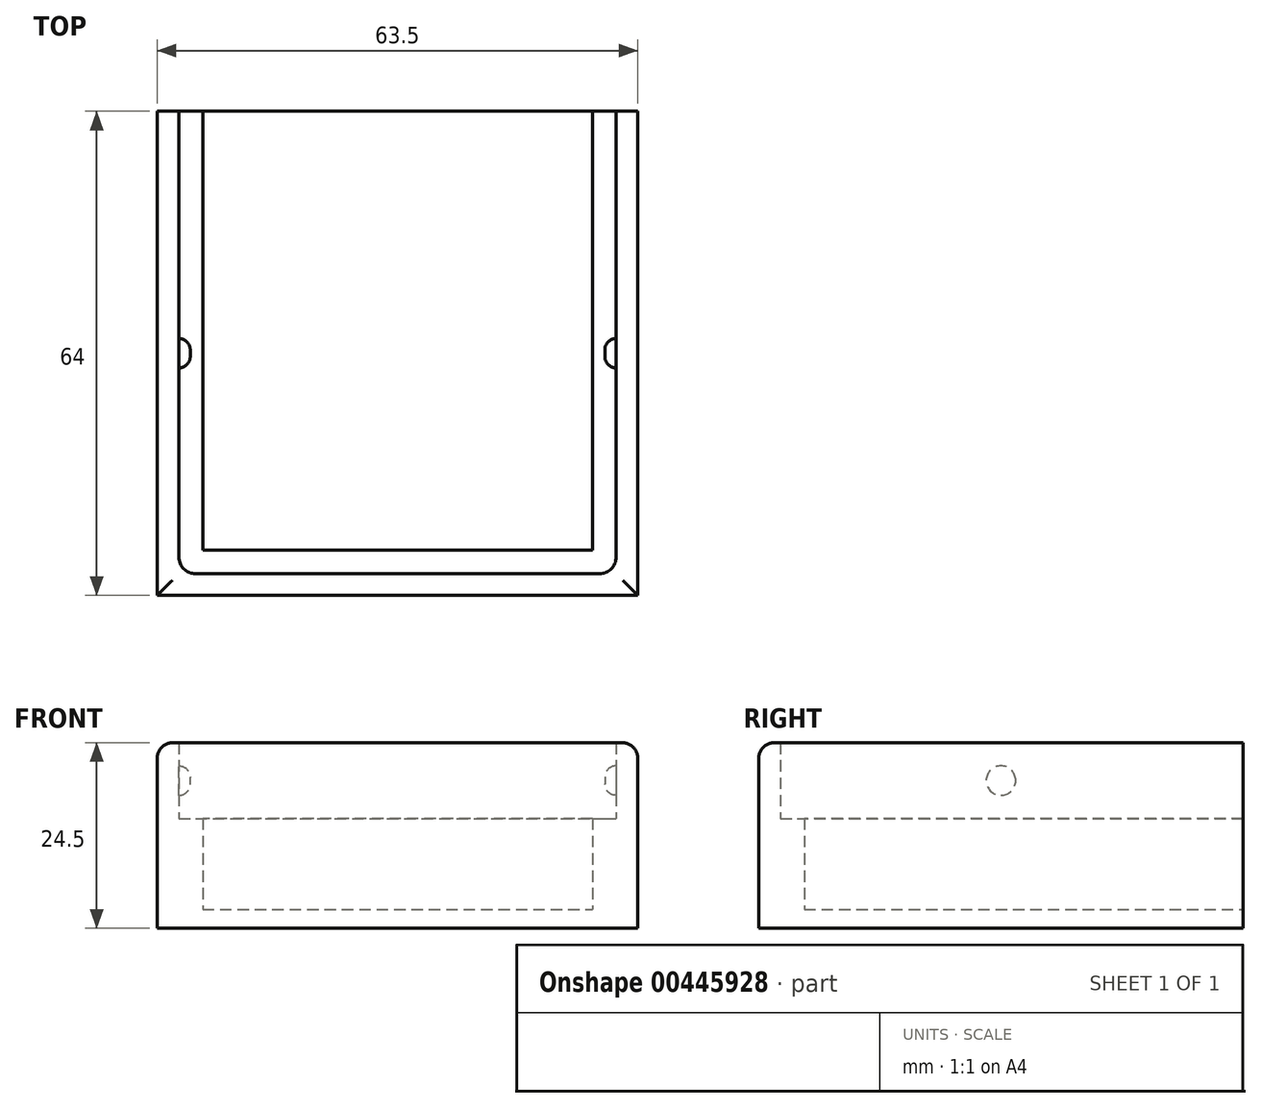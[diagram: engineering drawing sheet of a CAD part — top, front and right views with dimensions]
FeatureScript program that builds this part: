
annotation { "Feature Type Name" : "Feature", "Feature Type Description" : "" }
export const myFeature = defineFeature(function(context is Context, id is Id, definition is map)
    precondition{}
    {
        {
            var Q0;
            Q0=qCreatedBy(makeId("Top.planeOp"),FACE);
            var sketch = newSketch(context, id + "F0", { "sketchPlane" : qUnion([Q0])});
            skLineSegment(sketch, "E0.bottom", {"start": v(-31.75, 32) * mm, "end": v(31.75, 32) * mm});
            skLineSegment(sketch, "E0.top", {"start": v(-31.75, -32) * mm, "end": v(31.75, -32) * mm});
            skLineSegment(sketch, "E0.left", {"start": v(-31.75, 32) * mm, "end": v(-31.75, -32) * mm});
            skLineSegment(sketch, "E0.right", {"start": v(31.75, 32) * mm, "end": v(31.75, -32) * mm});
            skSolve(sketch);
        }
        {
            var Q0;
            Q0=makeQuery(id+"F0.imprint","IMPRINT",FACE,{"disambiguationData":[TD([[makeQuery(id+"F0.imprint","IMPRINT",EDGE,{"derivedFrom":sQuery(id+"F0.wireOp",EDGE,"E0.bottom")}),-1.0]])]});
            extrude(context, id + "F1", {"entities" : qUnion([Q0]), "depth" : 2.5 * mm});
        }
        {
            var Q0;
            Q0=makeQuery(id+"F1.opExtrude","CAP_FACE",FACE,{"disambiguationData":[OSD([sQuery(id+"F0.wireOp",EDGE,"E0.bottom"),sQuery(id+"F0.wireOp",EDGE,"E0.top"),sQuery(id+"F0.wireOp",EDGE,"E0.left"),sQuery(id+"F0.wireOp",EDGE,"E0.right")])],"isStart":false});
            var sketch = newSketch(context, id + "F2", { "sketchPlane" : qUnion([Q0])});
            skLineSegment(sketch, "E1", {"start": v(-31.75, 32) * mm, "end": v(-31.75, -32) * mm});
            skLineSegment(sketch, "E2", {"start": v(-31.75, -32) * mm, "end": v(31.75, -32) * mm});
            skLineSegment(sketch, "E3", {"start": v(31.75, -32) * mm, "end": v(31.75, 32) * mm});
            skLineSegment(sketch, "E4", {"start": v(31.75, 32) * mm, "end": v(25.75, 32) * mm});
            skLineSegment(sketch, "E5", {"start": v(25.75, 32) * mm, "end": v(25.75, -26) * mm});
            skLineSegment(sketch, "E6", {"start": v(25.75, -26) * mm, "end": v(-25.75, -26) * mm});
            skLineSegment(sketch, "E7", {"start": v(-25.75, -26) * mm, "end": v(-25.75, 32) * mm});
            skLineSegment(sketch, "E8", {"start": v(-25.75, 32) * mm, "end": v(-31.75, 32) * mm});
            skSolve(sketch);
        }
        {
            var Q0;
            Q0 = qSketchRegion(id + "F2", true);
            extrude(context, id + "F3", {"entities" : qUnion([Q0]), "operationType" : NewBodyOperationType.ADD, "depth" : 12 * mm});
        }
        {
            var Q0;
            Q0=makeQuery(id+"F3.opExtrude","CAP_FACE",FACE,{"disambiguationData":[OSD([sQuery(id+"F2.wireOp",EDGE,"E1"),sQuery(id+"F2.wireOp",EDGE,"E2"),sQuery(id+"F2.wireOp",EDGE,"E3"),sQuery(id+"F2.wireOp",EDGE,"E4"),sQuery(id+"F2.wireOp",EDGE,"E5"),sQuery(id+"F2.wireOp",EDGE,"E6"),sQuery(id+"F2.wireOp",EDGE,"E7"),sQuery(id+"F2.wireOp",EDGE,"E8")])],"isStart":false});
            var sketch = newSketch(context, id + "F4", { "sketchPlane" : qUnion([Q0])});
            skLineSegment(sketch, "E9", {"start": v(-31.75, 32) * mm, "end": v(-31.75, -32) * mm});
            skLineSegment(sketch, "E10", {"start": v(-31.75, -32) * mm, "end": v(31.75, -32) * mm});
            skLineSegment(sketch, "E11", {"start": v(31.75, -32) * mm, "end": v(31.75, 32) * mm});
            skLineSegment(sketch, "E12", {"start": v(-28.9, 32) * mm, "end": v(-28.9, -29.15) * mm});
            skLineSegment(sketch, "E13", {"start": v(-28.9, -29.15) * mm, "end": v(28.9, -29.15) * mm});
            skLineSegment(sketch, "E14", {"start": v(28.9, -29.15) * mm, "end": v(28.9, 32) * mm});
            skLineSegment(sketch, "E15", {"start": v(-31.75, 32) * mm, "end": v(-28.9, 32) * mm});
            skLineSegment(sketch, "E16", {"start": v(31.75, 32) * mm, "end": v(28.9, 32) * mm});
            skSolve(sketch);
        }
        {
            var Q0;
            Q0 = qSketchRegion(id + "F4", true);
            extrude(context, id + "F5", {"entities" : qUnion([Q0]), "operationType" : NewBodyOperationType.ADD, "depth" : 10 * mm});
        }
        {
            var Q0;
            Q0=makeQuery(id+"F5.opExtrude","SWEPT_EDGE",EDGE,{"disambiguationData":[OSD([sQuery(id+"F4.wireOp",EDGE,"E12"),sQuery(id+"F4.wireOp",EDGE,"E13")])]});
            var Q1;
            Q1=makeQuery(id+"F5.opExtrude","SWEPT_EDGE",EDGE,{"disambiguationData":[OSD([sQuery(id+"F4.wireOp",EDGE,"E13"),sQuery(id+"F4.wireOp",EDGE,"E14")])]});
            fillet(context, id + "F6", {"entities" : qUnion([Q0, Q1]), "radius" : 2.2 * mm, "tangentPropagation" : true, "allowEdgeOverflow" : false});
        }
        {
            var Q0;
            Q0=makeQuery(id+"F5.opExtrude","CAP_EDGE",EDGE,{"disambiguationData":[OSD([sQuery(id+"F4.wireOp",EDGE,"E9")])],"isStart":false});
            var Q1;
            Q1=makeQuery(id+"F5.opExtrude","CAP_EDGE",EDGE,{"disambiguationData":[OSD([sQuery(id+"F4.wireOp",EDGE,"E10")])],"isStart":false});
            var Q2;
            Q2=makeQuery(id+"F5.opExtrude","CAP_EDGE",EDGE,{"disambiguationData":[OSD([sQuery(id+"F4.wireOp",EDGE,"E11")])],"isStart":false});
            fillet(context, id + "F7", {"entities" : qUnion([Q0, Q1, Q2]), "radius" : 2 * mm, "tangentPropagation" : true, "allowEdgeOverflow" : false});
        }
        {
            var Q0;
            Q0=makeQuery(id+"F5.opExtrude","SWEPT_FACE",FACE,{"disambiguationData":[OSD([sQuery(id+"F4.wireOp",EDGE,"E12")])]});
            var sketch = newSketch(context, id + "F8", { "sketchPlane" : qUnion([Q0])});
            skCircle(sketch, "E17", {"center": v(0, 19.5) * mm, "radius": 1.95 * mm});
            skSolve(sketch);
        }
        {
            var Q0;
            Q0=makeQuery(id+"F8.imprint","IMPRINT",FACE,{"disambiguationData":[TD([[makeQuery(id+"F8.imprint","IMPRINT",EDGE,{"derivedFrom":sQuery(id+"F8.wireOp",EDGE,"E17")}),1.0]])]});
            extrude(context, id + "F9", {"entities" : qUnion([Q0]), "operationType" : NewBodyOperationType.ADD, "depth" : 1.5 * mm});
        }
        {
            var Q0;
            Q0=makeQuery(id+"F9.opExtrude","CAP_EDGE",EDGE,{"disambiguationData":[OSD([sQuery(id+"F8.wireOp",EDGE,"E17")])],"isStart":false});
            fillet(context, id + "F10", {"entities" : qUnion([Q0]), "radius" : 1.5 * mm, "tangentPropagation" : true, "allowEdgeOverflow" : false});
        }
        {
            var Q0;
            Q0=makeQuery(id+"F5.opExtrude","SWEPT_FACE",FACE,{"disambiguationData":[OSD([sQuery(id+"F4.wireOp",EDGE,"E14")])]});
            var sketch = newSketch(context, id + "F11", { "sketchPlane" : qUnion([Q0])});
            skCircle(sketch, "E18", {"center": v(0, 19.5) * mm, "radius": 1.95 * mm});
            skSolve(sketch);
        }
        {
            var Q0;
            Q0=makeQuery(id+"F11.imprint","IMPRINT",FACE,{"disambiguationData":[TD([[makeQuery(id+"F11.imprint","IMPRINT",EDGE,{"derivedFrom":sQuery(id+"F11.wireOp",EDGE,"E18")}),1.0]])]});
            extrude(context, id + "F12", {"entities" : qUnion([Q0]), "operationType" : NewBodyOperationType.ADD, "depth" : 1.5 * mm});
        }
        {
            var Q0;
            Q0=makeQuery(id+"F12.opExtrude","CAP_EDGE",EDGE,{"disambiguationData":[OSD([sQuery(id+"F11.wireOp",EDGE,"E18")])],"isStart":false});
            fillet(context, id + "F13", {"entities" : qUnion([Q0]), "radius" : 1.5 * mm, "tangentPropagation" : true, "allowEdgeOverflow" : false});
        }
    });
